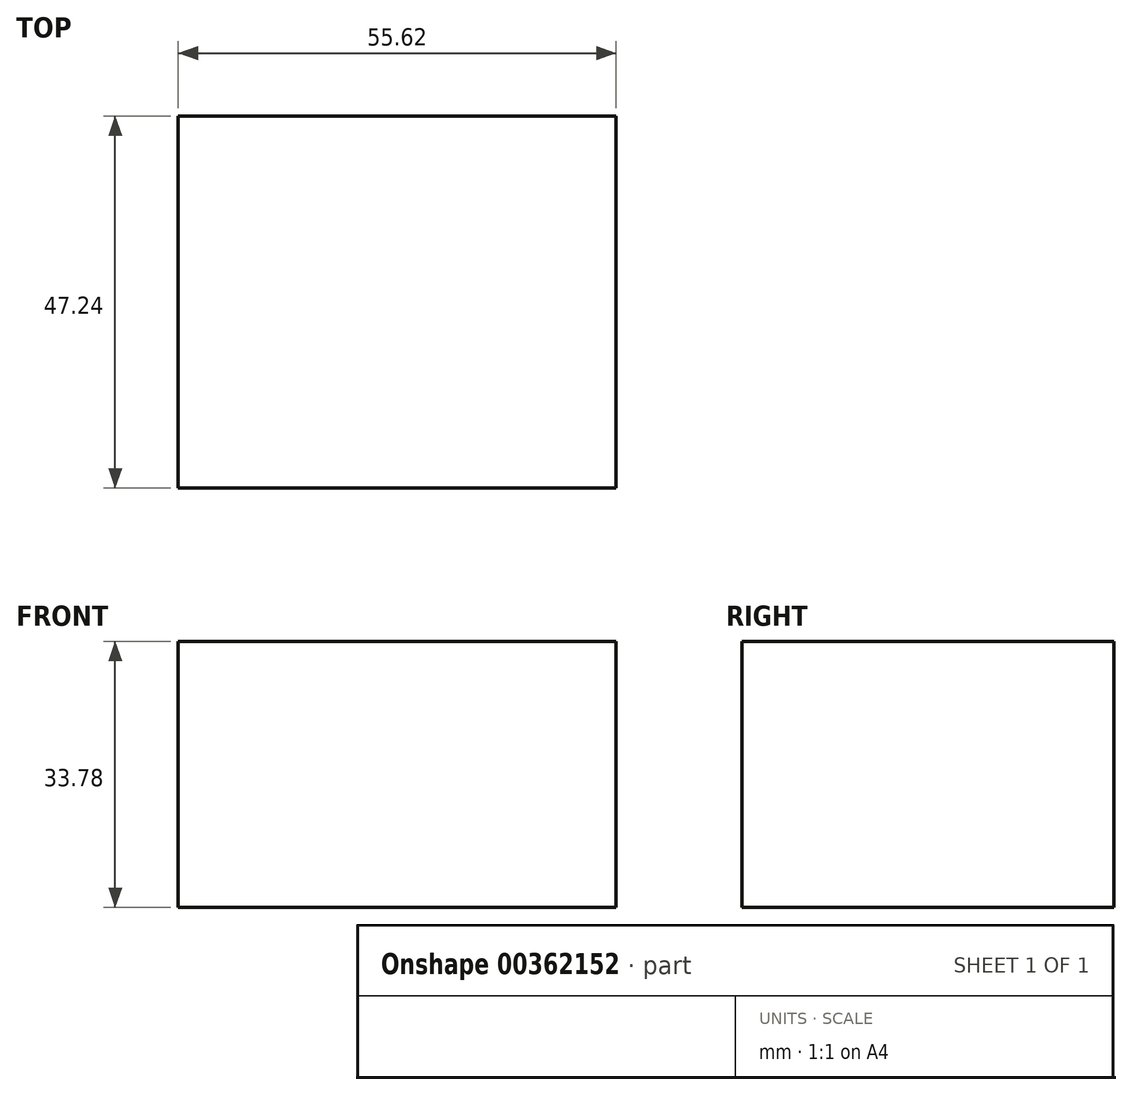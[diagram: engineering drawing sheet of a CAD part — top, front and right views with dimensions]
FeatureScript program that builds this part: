
annotation { "Feature Type Name" : "Feature", "Feature Type Description" : "" }
export const myFeature = defineFeature(function(context is Context, id is Id, definition is map)
    precondition{}
    {
        {
            var Q0;
            Q0=qCreatedBy(makeId("Top.planeOp"),FACE);
            var sketch = newSketch(context, id + "F0", { "sketchPlane" : qUnion([Q0])});
            skLineSegment(sketch, "E0.bottom", {"start": v(27.81, -23.62) * mm, "end": v(-27.81, -23.62) * mm});
            skLineSegment(sketch, "E0.top", {"start": v(27.81, 23.62) * mm, "end": v(-27.81, 23.62) * mm});
            skLineSegment(sketch, "E0.left", {"start": v(27.81, -23.62) * mm, "end": v(27.81, 23.62) * mm});
            skLineSegment(sketch, "E0.right", {"start": v(-27.81, -23.62) * mm, "end": v(-27.81, 23.62) * mm});
            skPoint(sketch, "E0.middle", {"position": v(0, 0) * mm});
            skSolve(sketch);
        }
        {
            var Q0;
            Q0=makeQuery(id+"F0.imprint","IMPRINT",FACE,{"disambiguationData":[TD([[makeQuery(id+"F0.imprint","IMPRINT",EDGE,{"derivedFrom":sQuery(id+"F0.wireOp",EDGE,"E0.bottom")}),-1.0]])]});
            extrude(context, id + "F1", {"entities" : qUnion([Q0]), "depth" : 33.78 * mm, "offsetDistance" : 25.4 * mm});
        }
    });
